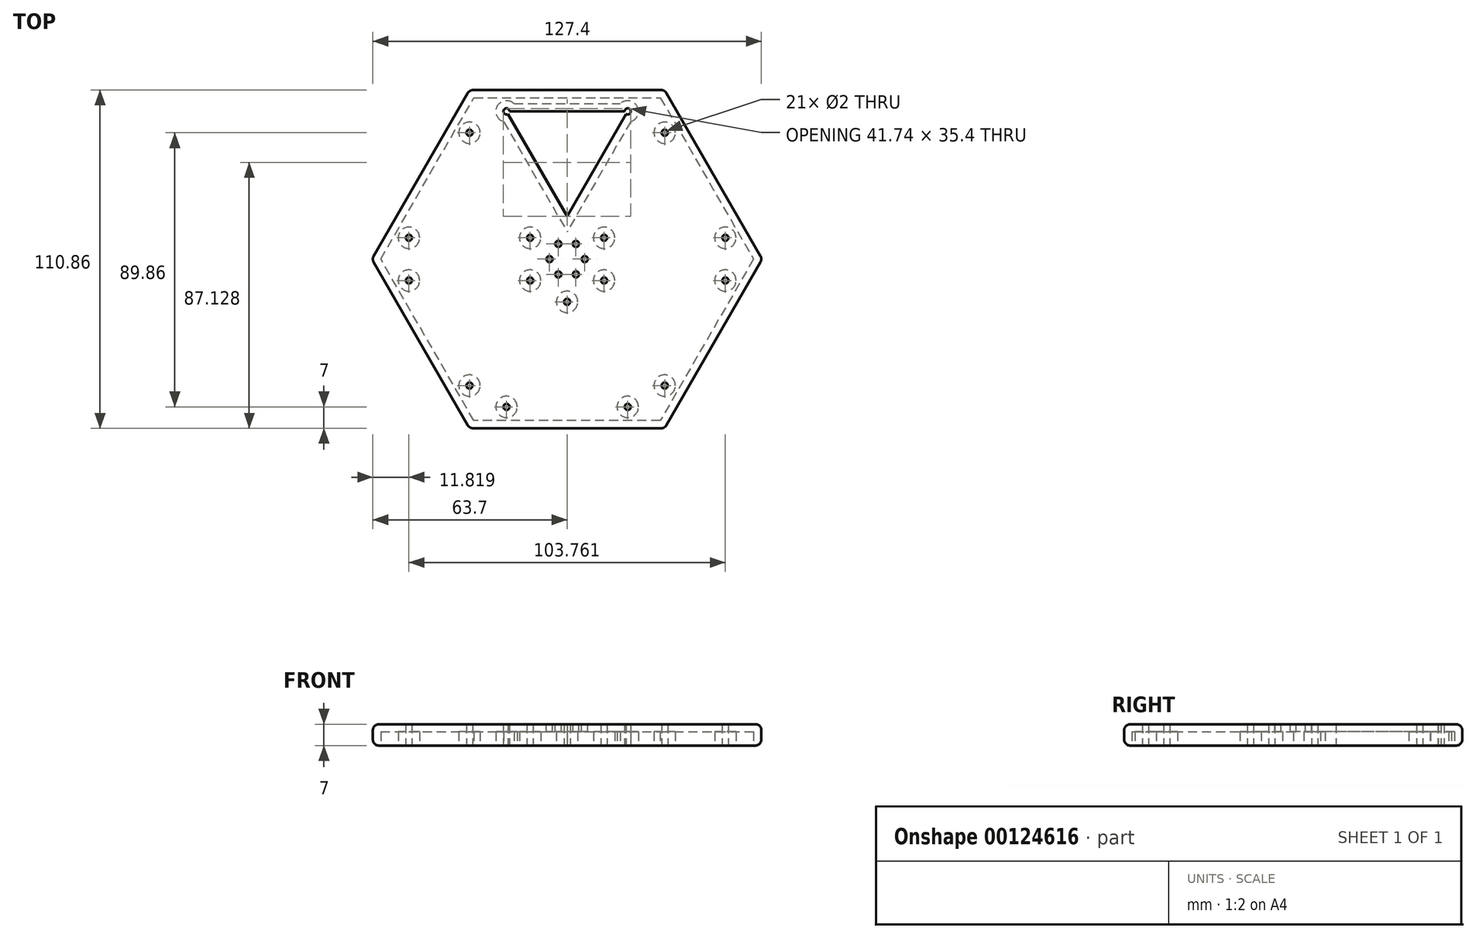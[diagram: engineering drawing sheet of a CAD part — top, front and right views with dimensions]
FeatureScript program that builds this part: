
annotation { "Feature Type Name" : "Feature", "Feature Type Description" : "" }
export const myFeature = defineFeature(function(context is Context, id is Id, definition is map)
    precondition{}
    {
        {
            var Q0;
            Q0=qCreatedBy(makeId("Top.planeOp"),FACE);
            var sketch = newSketch(context, id + "F0", { "sketchPlane" : qUnion([Q0])});
            skCircle(sketch, "E0.cCircle", {"center": v(0, 0) * mm, "radius": 55.43 * mm, "construction": true});
            skLineSegment(sketch, "E0.0", {"start": v(-32, 55.43) * mm, "end": v(32, 55.43) * mm});
            skLineSegment(sketch, "E0.1", {"start": v(32, 55.43) * mm, "end": v(64, 0) * mm});
            skLineSegment(sketch, "E0.2", {"start": v(64, 0) * mm, "end": v(32, -55.43) * mm});
            skLineSegment(sketch, "E0.3", {"start": v(32, -55.43) * mm, "end": v(-32, -55.43) * mm});
            skLineSegment(sketch, "E0.4", {"start": v(-32, -55.43) * mm, "end": v(-64, 0) * mm});
            skLineSegment(sketch, "E0.5", {"start": v(-64, 0) * mm, "end": v(-32, 55.43) * mm});
            skPoint(sketch, "E0.0.midPoint", {"position": v(0, 55.43) * mm});
            skLineSegment(sketch, "E1", {"start": v(0, 0) * mm, "end": v(0, 55.43) * mm});
            skLineSegment(sketch, "E2", {"start": v(-32, 55.43) * mm, "end": v(0, 0) * mm});
            skLineSegment(sketch, "E3", {"start": v(32, 55.43) * mm, "end": v(0, 0) * mm});
            skLineSegment(sketch, "E4.0", {"start": v(-19.88, 48.43) * mm, "end": v(0, 14) * mm});
            skLineSegment(sketch, "E4.1", {"start": v(-19.88, 48.43) * mm, "end": v(19.88, 48.43) * mm});
            skLineSegment(sketch, "E4.2", {"start": v(19.88, 48.43) * mm, "end": v(0, 14) * mm});
            skCircle(sketch, "E5", {"center": v(-19.88, 48.43) * mm, "radius": 1 * mm});
            skCircle(sketch, "E6", {"center": v(19.88, 48.43) * mm, "radius": 1 * mm});
            skCircle(sketch, "E7", {"center": v(0, 14) * mm, "radius": 1 * mm});
            skCircle(sketch, "E8.1.0", {"center": v(-51.88, 7) * mm, "radius": 1 * mm});
            skCircle(sketch, "E8.1.1", {"center": v(-32, 41.43) * mm, "radius": 1 * mm});
            skCircle(sketch, "E8.1.2", {"center": v(-12.12, 7) * mm, "radius": 1 * mm});
            skCircle(sketch, "E8.2.0", {"center": v(-32, -41.43) * mm, "radius": 1 * mm});
            skCircle(sketch, "E8.2.1", {"center": v(-51.88, -7) * mm, "radius": 1 * mm});
            skCircle(sketch, "E8.2.2", {"center": v(-12.12, -7) * mm, "radius": 1 * mm});
            skCircle(sketch, "E8.3.0", {"center": v(19.88, -48.43) * mm, "radius": 1 * mm});
            skCircle(sketch, "E8.3.1", {"center": v(-19.88, -48.43) * mm, "radius": 1 * mm});
            skCircle(sketch, "E8.3.2", {"center": v(0, -14) * mm, "radius": 1 * mm});
            skCircle(sketch, "E8.4.0", {"center": v(51.88, -7) * mm, "radius": 1 * mm});
            skCircle(sketch, "E8.4.1", {"center": v(32, -41.43) * mm, "radius": 1 * mm});
            skCircle(sketch, "E8.4.2", {"center": v(12.12, -7) * mm, "radius": 1 * mm});
            skCircle(sketch, "E8.5.0", {"center": v(32, 41.43) * mm, "radius": 1 * mm});
            skCircle(sketch, "E8.5.1", {"center": v(51.88, 7) * mm, "radius": 1 * mm});
            skCircle(sketch, "E8.5.2", {"center": v(12.12, 7) * mm, "radius": 1 * mm});
            skSolve(sketch);
        }
        {
            var Q0;
            Q0=qSketchRegion(id+"F0",true);
            var Q1;
            {var subQ1=sQuery(id+"F0.wireOp",EDGE,"E1");var subQ7=sQuery(id+"F0.wireOp",EDGE,"E7");var subQ9=makeQuery(id+"F0.imprint","INTERSECT",VERTEX,{"disambiguationData":[OD(1.0)],"derivedFrom":[subQ1,subQ7]});Q1=makeQuery(id+"F0.imprint","IMPRINT",FACE,{"disambiguationData":[TD([[makeQuery(id+"F0.imprint","IMPRINT",EDGE,{"disambiguationData":[TD([[subQ9,-1.0]])],"derivedFrom":subQ1}),1.0]])]});}
            var Q2;
            {var subQ3=sQuery(id+"F0.wireOp",EDGE,"E7");var subQ6=sQuery(id+"F0.wireOp",EDGE,"E1");var subQ9=makeQuery(id+"F0.imprint","INTERSECT",VERTEX,{"disambiguationData":[OD(1.0)],"derivedFrom":[subQ6,subQ3]});Q2=makeQuery(id+"F0.imprint","IMPRINT",FACE,{"disambiguationData":[TD([[makeQuery(id+"F0.imprint","IMPRINT",EDGE,{"disambiguationData":[TD([[subQ9,-1.0]])],"derivedFrom":subQ6}),-1.0]])]});}
            extrude(context, id + "F1", {"entities" : qUnion([Q0, Q1, Q2]), "depth" : 7 * mm});
        }
        {
            var Q0;
            Q0=makeQuery(id+"F1.opExtrude","CAP_FACE",FACE,{"disambiguationData":[OSD([sQuery(id+"F0.wireOp",EDGE,"E0.0"),sQuery(id+"F0.wireOp",EDGE,"E0.1"),sQuery(id+"F0.wireOp",EDGE,"E0.2"),sQuery(id+"F0.wireOp",EDGE,"E0.3"),sQuery(id+"F0.wireOp",EDGE,"E0.4"),sQuery(id+"F0.wireOp",EDGE,"E0.5"),sQuery(id+"F0.wireOp",EDGE,"E5"),sQuery(id+"F0.wireOp",EDGE,"E6"),sQuery(id+"F0.wireOp",EDGE,"E7"),sQuery(id+"F0.wireOp",EDGE,"E8.1.0"),sQuery(id+"F0.wireOp",EDGE,"E8.1.1"),sQuery(id+"F0.wireOp",EDGE,"E8.1.2"),sQuery(id+"F0.wireOp",EDGE,"E8.2.0"),sQuery(id+"F0.wireOp",EDGE,"E8.2.1"),sQuery(id+"F0.wireOp",EDGE,"E8.2.2"),sQuery(id+"F0.wireOp",EDGE,"E8.3.0"),sQuery(id+"F0.wireOp",EDGE,"E8.3.1"),sQuery(id+"F0.wireOp",EDGE,"E8.3.2"),sQuery(id+"F0.wireOp",EDGE,"E8.4.0"),sQuery(id+"F0.wireOp",EDGE,"E8.4.1"),sQuery(id+"F0.wireOp",EDGE,"E8.4.2"),sQuery(id+"F0.wireOp",EDGE,"E8.5.0"),sQuery(id+"F0.wireOp",EDGE,"E8.5.1"),sQuery(id+"F0.wireOp",EDGE,"E8.5.2")])],"isStart":true});
            shell(context, id + "F2", {"entities" : qUnion([Q0]), "thickness" : 2.5 * mm});
        }
        {
            var Q0;
            Q0=makeQuery(id+"F1.opExtrude","CAP_EDGE",EDGE,{"disambiguationData":[OSD([sQuery(id+"F0.wireOp",EDGE,"E0.3")])],"isStart":false});
            var Q1;
            Q1=makeQuery(id+"F1.opExtrude","CAP_EDGE",EDGE,{"disambiguationData":[OSD([sQuery(id+"F0.wireOp",EDGE,"E0.4")])],"isStart":false});
            var Q2;
            Q2=makeQuery(id+"F1.opExtrude","CAP_EDGE",EDGE,{"disambiguationData":[OSD([sQuery(id+"F0.wireOp",EDGE,"E0.5")])],"isStart":false});
            var Q3;
            Q3=makeQuery(id+"F1.opExtrude","CAP_EDGE",EDGE,{"disambiguationData":[OSD([sQuery(id+"F0.wireOp",EDGE,"E0.0")])],"isStart":false});
            var Q4;
            Q4=makeQuery(id+"F1.opExtrude","CAP_EDGE",EDGE,{"disambiguationData":[OSD([sQuery(id+"F0.wireOp",EDGE,"E0.1")])],"isStart":false});
            var Q5;
            Q5=makeQuery(id+"F1.opExtrude","CAP_EDGE",EDGE,{"disambiguationData":[OSD([sQuery(id+"F0.wireOp",EDGE,"E0.2")])],"isStart":false});
            var Q6;
            Q6=makeQuery(id+"F1.opExtrude","CAP_EDGE",EDGE,{"disambiguationData":[OSD([sQuery(id+"F0.wireOp",EDGE,"E0.2")])],"isStart":true});
            var Q7;
            Q7=makeQuery(id+"F1.opExtrude","CAP_EDGE",EDGE,{"disambiguationData":[OSD([sQuery(id+"F0.wireOp",EDGE,"E0.3")])],"isStart":true});
            var Q8;
            Q8=makeQuery(id+"F1.opExtrude","SWEPT_EDGE",EDGE,{"disambiguationData":[OSD([sQuery(id+"F0.wireOp",EDGE,"E0.2"),sQuery(id+"F0.wireOp",EDGE,"E0.3")])]});
            var Q9;
            Q9=makeQuery(id+"F1.opExtrude","SWEPT_EDGE",EDGE,{"disambiguationData":[OSD([sQuery(id+"F0.wireOp",EDGE,"E0.1"),sQuery(id+"F0.wireOp",EDGE,"E0.2")])]});
            var Q10;
            Q10=makeQuery(id+"F1.opExtrude","CAP_EDGE",EDGE,{"disambiguationData":[OSD([sQuery(id+"F0.wireOp",EDGE,"E0.1")])],"isStart":true});
            var Q11;
            Q11=makeQuery(id+"F1.opExtrude","SWEPT_EDGE",EDGE,{"disambiguationData":[OSD([sQuery(id+"F0.wireOp",EDGE,"E0.0"),sQuery(id+"F0.wireOp",EDGE,"E0.1"),sQuery(id+"F0.wireOp",EDGE,"E3")])]});
            var Q12;
            Q12=makeQuery(id+"F1.opExtrude","CAP_EDGE",EDGE,{"disambiguationData":[OSD([sQuery(id+"F0.wireOp",EDGE,"E0.0")])],"isStart":true});
            var Q13;
            Q13=makeQuery(id+"F1.opExtrude","SWEPT_EDGE",EDGE,{"disambiguationData":[OSD([sQuery(id+"F0.wireOp",EDGE,"E0.0"),sQuery(id+"F0.wireOp",EDGE,"E0.5"),sQuery(id+"F0.wireOp",EDGE,"E2")])]});
            var Q14;
            Q14=makeQuery(id+"F1.opExtrude","CAP_EDGE",EDGE,{"disambiguationData":[OSD([sQuery(id+"F0.wireOp",EDGE,"E0.5")])],"isStart":true});
            var Q15;
            Q15=makeQuery(id+"F1.opExtrude","SWEPT_EDGE",EDGE,{"disambiguationData":[OSD([sQuery(id+"F0.wireOp",EDGE,"E0.4"),sQuery(id+"F0.wireOp",EDGE,"E0.5")])]});
            var Q16;
            Q16=makeQuery(id+"F1.opExtrude","CAP_EDGE",EDGE,{"disambiguationData":[OSD([sQuery(id+"F0.wireOp",EDGE,"E0.4")])],"isStart":true});
            var Q17;
            Q17=makeQuery(id+"F1.opExtrude","SWEPT_EDGE",EDGE,{"disambiguationData":[OSD([sQuery(id+"F0.wireOp",EDGE,"E0.3"),sQuery(id+"F0.wireOp",EDGE,"E0.4")])]});
            fillet(context, id + "F3", {"entities" : qUnion([Q0, Q1, Q2, Q3, Q4, Q5, Q6, Q7, Q8, Q9, Q10, Q11, Q12, Q13, Q14, Q15, Q16, Q17]), "radius" : 2 * mm, "tangentPropagation" : true, "allowEdgeOverflow" : false});
        }
        {
            var Q0;
            Q0=makeQuery(id+"F1.opExtrude","CAP_FACE",FACE,{"disambiguationData":[OSD([sQuery(id+"F0.wireOp",EDGE,"E0.0"),sQuery(id+"F0.wireOp",EDGE,"E0.1"),sQuery(id+"F0.wireOp",EDGE,"E0.2"),sQuery(id+"F0.wireOp",EDGE,"E0.3"),sQuery(id+"F0.wireOp",EDGE,"E0.4"),sQuery(id+"F0.wireOp",EDGE,"E0.5"),sQuery(id+"F0.wireOp",EDGE,"E5"),sQuery(id+"F0.wireOp",EDGE,"E6"),sQuery(id+"F0.wireOp",EDGE,"E7"),sQuery(id+"F0.wireOp",EDGE,"E8.1.0"),sQuery(id+"F0.wireOp",EDGE,"E8.1.1"),sQuery(id+"F0.wireOp",EDGE,"E8.1.2"),sQuery(id+"F0.wireOp",EDGE,"E8.2.0"),sQuery(id+"F0.wireOp",EDGE,"E8.2.1"),sQuery(id+"F0.wireOp",EDGE,"E8.2.2"),sQuery(id+"F0.wireOp",EDGE,"E8.3.0"),sQuery(id+"F0.wireOp",EDGE,"E8.3.1"),sQuery(id+"F0.wireOp",EDGE,"E8.3.2"),sQuery(id+"F0.wireOp",EDGE,"E8.4.0"),sQuery(id+"F0.wireOp",EDGE,"E8.4.1"),sQuery(id+"F0.wireOp",EDGE,"E8.4.2"),sQuery(id+"F0.wireOp",EDGE,"E8.5.0"),sQuery(id+"F0.wireOp",EDGE,"E8.5.1"),sQuery(id+"F0.wireOp",EDGE,"E8.5.2")])],"isStart":false});
            var sketch = newSketch(context, id + "F4", { "sketchPlane" : qUnion([Q0])});
            skCircle(sketch, "E9.cCircle", {"center": v(0, 0) * mm, "radius": 5 * mm, "construction": true});
            skLineSegment(sketch, "E9.0", {"start": v(-2.89, 5) * mm, "end": v(2.89, 5) * mm});
            skLineSegment(sketch, "E9.1", {"start": v(2.89, 5) * mm, "end": v(5.77, 0) * mm});
            skLineSegment(sketch, "E9.2", {"start": v(5.77, 0) * mm, "end": v(2.89, -5) * mm});
            skLineSegment(sketch, "E9.3", {"start": v(2.89, -5) * mm, "end": v(-2.89, -5) * mm});
            skLineSegment(sketch, "E9.4", {"start": v(-2.89, -5) * mm, "end": v(-5.77, 0) * mm});
            skLineSegment(sketch, "E9.5", {"start": v(-5.77, 0) * mm, "end": v(-2.89, 5) * mm});
            skPoint(sketch, "E9.0.midPoint", {"position": v(0, 5) * mm});
            skCircle(sketch, "E10", {"center": v(-2.89, 5) * mm, "radius": 1 * mm});
            skCircle(sketch, "E11.1.0", {"center": v(-5.77, 0) * mm, "radius": 1 * mm});
            skCircle(sketch, "E11.2.0", {"center": v(-2.89, -5) * mm, "radius": 1 * mm});
            skCircle(sketch, "E11.3.0", {"center": v(2.89, -5) * mm, "radius": 1 * mm});
            skCircle(sketch, "E11.4.0", {"center": v(5.77, 0) * mm, "radius": 1 * mm});
            skCircle(sketch, "E11.5.0", {"center": v(2.89, 5) * mm, "radius": 1 * mm});
            skSolve(sketch);
        }
        {
            var Q0;
            {var subQ0=sQuery(id+"F4.wireOp",EDGE,"E9.5");var subQ1=sQuery(id+"F4.wireOp",EDGE,"E9.0");var subQ2=makeQuery(id+"F4.imprint","INTERSECT",VERTEX,{"derivedFrom":[subQ1,subQ0]});Q0=makeQuery(id+"F4.imprint","IMPRINT",FACE,{"disambiguationData":[TD([[makeQuery(id+"F4.imprint","IMPRINT",EDGE,{"disambiguationData":[TD([[subQ2,-1.0]])],"derivedFrom":subQ1}),-1.0]])]});}
            var Q1;
            {var subQ0=sQuery(id+"F4.wireOp",EDGE,"E9.5");var subQ1=sQuery(id+"F4.wireOp",EDGE,"E9.0");var subQ2=makeQuery(id+"F4.imprint","INTERSECT",VERTEX,{"derivedFrom":[subQ1,subQ0]});Q1=makeQuery(id+"F4.imprint","IMPRINT",FACE,{"disambiguationData":[TD([[makeQuery(id+"F4.imprint","IMPRINT",EDGE,{"disambiguationData":[TD([[subQ2,-1.0]])],"derivedFrom":subQ1}),1.0]])]});}
            extrude(context, id + "F5", {"entities" : qUnion([Q0, Q1]), "operationType" : NewBodyOperationType.REMOVE, "oppositeDirection" : true, "depth" : 25 * mm});
        }
        {
            var Q0;
            {var subQ0=sQuery(id+"F4.wireOp",EDGE,"E9.5");var subQ1=sQuery(id+"F4.wireOp",EDGE,"E9.0");var subQ2=makeQuery(id+"F4.imprint","INTERSECT",VERTEX,{"derivedFrom":[subQ1,subQ0]});Q0=makeQuery(id+"F4.imprint","IMPRINT",FACE,{"disambiguationData":[TD([[makeQuery(id+"F4.imprint","IMPRINT",EDGE,{"disambiguationData":[TD([[subQ2,-1.0]])],"derivedFrom":subQ1}),1.0]])]});}
            var Q1;
            {var subQ0=sQuery(id+"F4.wireOp",EDGE,"E9.5");var subQ1=sQuery(id+"F4.wireOp",EDGE,"E9.0");var subQ2=makeQuery(id+"F4.imprint","INTERSECT",VERTEX,{"derivedFrom":[subQ1,subQ0]});Q1=makeQuery(id+"F4.imprint","IMPRINT",FACE,{"disambiguationData":[TD([[makeQuery(id+"F4.imprint","IMPRINT",EDGE,{"disambiguationData":[TD([[subQ2,-1.0]])],"derivedFrom":subQ1}),-1.0]])]});}
            var Q2;
            {var subQ0=sQuery(id+"F4.wireOp",EDGE,"E9.5");var subQ1=sQuery(id+"F4.wireOp",EDGE,"E9.4");var subQ2=makeQuery(id+"F4.imprint","INTERSECT",VERTEX,{"derivedFrom":[subQ1,subQ0]});Q2=makeQuery(id+"F4.imprint","IMPRINT",FACE,{"disambiguationData":[TD([[makeQuery(id+"F4.imprint","IMPRINT",EDGE,{"disambiguationData":[TD([[subQ2,1.0]])],"derivedFrom":subQ1}),1.0]])]});}
            var Q3;
            {var subQ0=sQuery(id+"F4.wireOp",EDGE,"E9.5");var subQ1=sQuery(id+"F4.wireOp",EDGE,"E9.4");var subQ2=makeQuery(id+"F4.imprint","INTERSECT",VERTEX,{"derivedFrom":[subQ1,subQ0]});Q3=makeQuery(id+"F4.imprint","IMPRINT",FACE,{"disambiguationData":[TD([[makeQuery(id+"F4.imprint","IMPRINT",EDGE,{"disambiguationData":[TD([[subQ2,1.0]])],"derivedFrom":subQ1}),-1.0]])]});}
            var Q4;
            {var subQ0=sQuery(id+"F4.wireOp",EDGE,"E9.4");var subQ1=sQuery(id+"F4.wireOp",EDGE,"E9.3");var subQ2=makeQuery(id+"F4.imprint","INTERSECT",VERTEX,{"derivedFrom":[subQ1,subQ0]});Q4=makeQuery(id+"F4.imprint","IMPRINT",FACE,{"disambiguationData":[TD([[makeQuery(id+"F4.imprint","IMPRINT",EDGE,{"disambiguationData":[TD([[subQ2,1.0]])],"derivedFrom":subQ1}),1.0]])]});}
            var Q5;
            {var subQ0=sQuery(id+"F4.wireOp",EDGE,"E9.4");var subQ1=sQuery(id+"F4.wireOp",EDGE,"E9.3");var subQ2=makeQuery(id+"F4.imprint","INTERSECT",VERTEX,{"derivedFrom":[subQ1,subQ0]});Q5=makeQuery(id+"F4.imprint","IMPRINT",FACE,{"disambiguationData":[TD([[makeQuery(id+"F4.imprint","IMPRINT",EDGE,{"disambiguationData":[TD([[subQ2,1.0]])],"derivedFrom":subQ1}),-1.0]])]});}
            var Q6;
            {var subQ0=sQuery(id+"F4.wireOp",EDGE,"E9.3");var subQ1=sQuery(id+"F4.wireOp",EDGE,"E9.2");var subQ2=makeQuery(id+"F4.imprint","INTERSECT",VERTEX,{"derivedFrom":[subQ1,subQ0]});Q6=makeQuery(id+"F4.imprint","IMPRINT",FACE,{"disambiguationData":[TD([[makeQuery(id+"F4.imprint","IMPRINT",EDGE,{"disambiguationData":[TD([[subQ2,1.0]])],"derivedFrom":subQ1}),1.0]])]});}
            var Q7;
            {var subQ0=sQuery(id+"F4.wireOp",EDGE,"E9.3");var subQ1=sQuery(id+"F4.wireOp",EDGE,"E9.2");var subQ2=makeQuery(id+"F4.imprint","INTERSECT",VERTEX,{"derivedFrom":[subQ1,subQ0]});Q7=makeQuery(id+"F4.imprint","IMPRINT",FACE,{"disambiguationData":[TD([[makeQuery(id+"F4.imprint","IMPRINT",EDGE,{"disambiguationData":[TD([[subQ2,1.0]])],"derivedFrom":subQ1}),-1.0]])]});}
            var Q8;
            {var subQ0=sQuery(id+"F4.wireOp",EDGE,"E9.2");var subQ1=sQuery(id+"F4.wireOp",EDGE,"E9.1");var subQ2=makeQuery(id+"F4.imprint","INTERSECT",VERTEX,{"derivedFrom":[subQ1,subQ0]});Q8=makeQuery(id+"F4.imprint","IMPRINT",FACE,{"disambiguationData":[TD([[makeQuery(id+"F4.imprint","IMPRINT",EDGE,{"disambiguationData":[TD([[subQ2,1.0]])],"derivedFrom":subQ1}),1.0]])]});}
            var Q9;
            {var subQ0=sQuery(id+"F4.wireOp",EDGE,"E9.2");var subQ1=sQuery(id+"F4.wireOp",EDGE,"E9.1");var subQ2=makeQuery(id+"F4.imprint","INTERSECT",VERTEX,{"derivedFrom":[subQ1,subQ0]});Q9=makeQuery(id+"F4.imprint","IMPRINT",FACE,{"disambiguationData":[TD([[makeQuery(id+"F4.imprint","IMPRINT",EDGE,{"disambiguationData":[TD([[subQ2,1.0]])],"derivedFrom":subQ1}),-1.0]])]});}
            var Q10;
            {var subQ0=sQuery(id+"F4.wireOp",EDGE,"E9.1");var subQ1=sQuery(id+"F4.wireOp",EDGE,"E9.0");var subQ2=makeQuery(id+"F4.imprint","INTERSECT",VERTEX,{"derivedFrom":[subQ1,subQ0]});Q10=makeQuery(id+"F4.imprint","IMPRINT",FACE,{"disambiguationData":[TD([[makeQuery(id+"F4.imprint","IMPRINT",EDGE,{"disambiguationData":[TD([[subQ2,1.0]])],"derivedFrom":subQ1}),-1.0]])]});}
            var Q11;
            {var subQ0=sQuery(id+"F4.wireOp",EDGE,"E9.1");var subQ1=sQuery(id+"F4.wireOp",EDGE,"E9.0");var subQ2=makeQuery(id+"F4.imprint","INTERSECT",VERTEX,{"derivedFrom":[subQ1,subQ0]});Q11=makeQuery(id+"F4.imprint","IMPRINT",FACE,{"disambiguationData":[TD([[makeQuery(id+"F4.imprint","IMPRINT",EDGE,{"disambiguationData":[TD([[subQ2,1.0]])],"derivedFrom":subQ1}),1.0]])]});}
            var Q12;
            Q12=sQuery(id+"F4.wireOp",EDGE,"E11.1.0");
            var Q13;
            Q13=sQuery(id+"F4.wireOp",EDGE,"E11.2.0");
            var Q14;
            Q14=sQuery(id+"F4.wireOp",EDGE,"E11.3.0");
            var Q15;
            Q15=sQuery(id+"F4.wireOp",EDGE,"E11.4.0");
            var Q16;
            Q16=sQuery(id+"F4.wireOp",EDGE,"E11.5.0");
            var Q17;
            Q17=sQuery(id+"F4.wireOp",EDGE,"E10");
            extrude(context, id + "F6", {"entities" : qUnion([Q0, Q1, Q2, Q3, Q4, Q5, Q6, Q7, Q8, Q9, Q10, Q11]), "operationType" : NewBodyOperationType.REMOVE, "surfaceEntities" : qUnion([Q12, Q13, Q14, Q15, Q16, Q17]), "oppositeDirection" : true, "depth" : 25 * mm});
        }
    });
